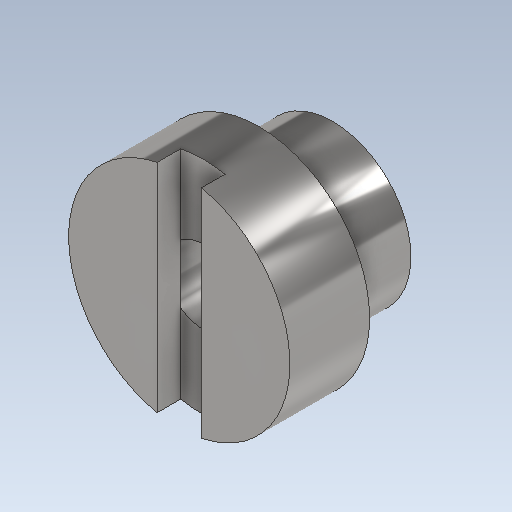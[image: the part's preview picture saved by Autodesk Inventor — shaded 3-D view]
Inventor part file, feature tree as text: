
AUTODESK INVENTOR PART (.ipt)
format: ipt  version: 2020 (Build 240168000, 168)  size: 154,112 bytes
history: native  units: in
note: dims shown in document units (in); Inventor stores cm internally (conversion verified against a paired STEP export)
features: extrude x4, sketch x4
ambient origin geometry x8: Origin, YZ Plane, XZ Plane, XY Plane, X Axis, Y Axis, Z Axis, Center Point
bodies: Solid1 (feature_tree)
feature tree (8):
  extrude  "Extrusion1"  Depth=2.126in TaperAngle=0.0deg
  extrude  "Extrusion2"  Depth=1.1811in
  extrude  "Extrusion3"  Depth=2.9528in
  extrude  "Extrusion4"  Depth=3.4646in
  sketch  "Sketch1"  dims[d0=5.9055in d1=2.126in d2=0.0in]
  sketch  "Sketch2"  dims[d3=1.1811in d4=0.5906in]
  sketch  "Sketch3"  dims[d5=2.9528in d6=2.9528in]
  sketch  "Sketch4"  dims[d7=0.6299in d8=0.0in d9=4.1732in d10=1.9685in d11=0.0in d12=1.9685in d13=3.4646in d14=0.0in]
